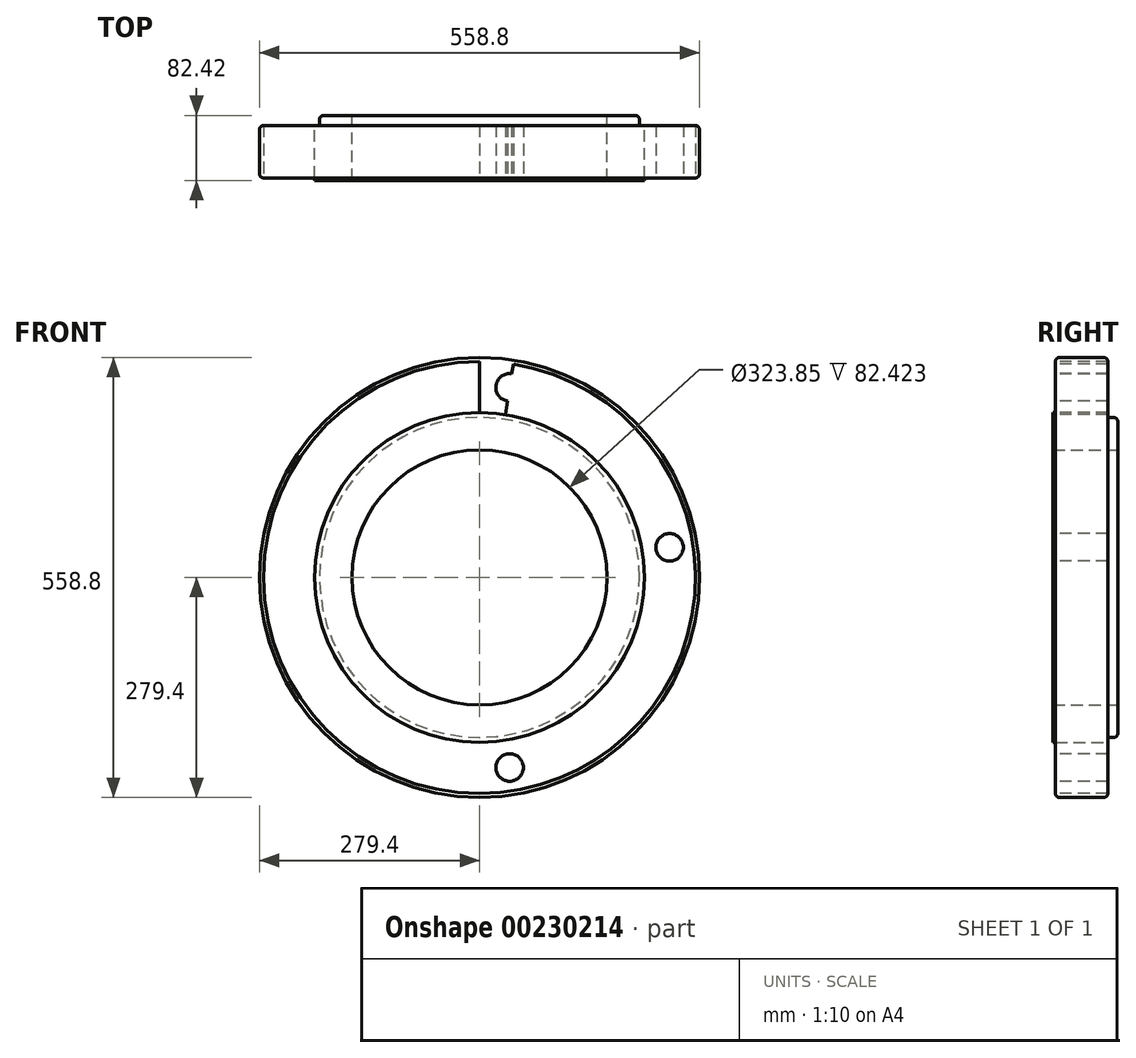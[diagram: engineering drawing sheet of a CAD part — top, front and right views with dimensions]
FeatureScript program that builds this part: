
annotation { "Feature Type Name" : "Feature", "Feature Type Description" : "" }
export const myFeature = defineFeature(function(context is Context, id is Id, definition is map)
    precondition{}
    {
        {
            var Q0;
            Q0=qCreatedBy(makeId("Front.planeOp"),FACE);
            var sketch = newSketch(context, id + "F0", { "sketchPlane" : qUnion([Q0])});
            skCircle(sketch, "E0", {"center": v(0, 0) * mm, "radius": 161.93 * mm});
            skCircle(sketch, "E1", {"center": v(0, 0) * mm, "radius": 279.4 * mm});
            skSolve(sketch);
        }
        {
            var Q0;
            Q0 = qSketchRegion(id + "F0", true);
            extrude(context, id + "F1", {"entities" : qUnion([Q0]), "depth" : 66.55 * mm});
        }
        {
            var Q0;
            Q0=makeQuery(id+"F1.opExtrude","CAP_FACE",FACE,{"disambiguationData":[OSD([sQuery(id+"F0.wireOp",EDGE,"E0"),sQuery(id+"F0.wireOp",EDGE,"E1")])],"isStart":false});
            var sketch = newSketch(context, id + "F2", { "sketchPlane" : qUnion([Q0])});
            skCircle(sketch, "E2", {"center": v(0, 0) * mm, "radius": 209.55 * mm});
            skCircle(sketch, "E3", {"center": v(0, 0) * mm, "radius": 161.93 * mm});
            skSolve(sketch);
        }
        {
            var Q0;
            Q0 = qSketchRegion(id + "F2", true);
            extrude(context, id + "F3", {"entities" : qUnion([Q0]), "operationType" : NewBodyOperationType.ADD, "depth" : 3.17 * mm});
        }
        {
            var Q0;
            Q0=makeQuery(id+"F1.opExtrude","CAP_FACE",FACE,{"disambiguationData":[OSD([sQuery(id+"F0.wireOp",EDGE,"E0"),sQuery(id+"F0.wireOp",EDGE,"E1")])],"isStart":true});
            var sketch = newSketch(context, id + "F4", { "sketchPlane" : qUnion([Q0])});
            skCircle(sketch, "E4", {"center": v(0, 0) * mm, "radius": 203.2 * mm});
            skCircle(sketch, "E5", {"center": v(0, 0) * mm, "radius": 161.93 * mm});
            skSolve(sketch);
        }
        {
            var Q0;
            Q0 = qSketchRegion(id + "F4", true);
            extrude(context, id + "F5", {"entities" : qUnion([Q0]), "operationType" : NewBodyOperationType.ADD, "depth" : 12.7 * mm});
        }
        {
            var Q0;
            Q0=makeQuery(id+"F1.opExtrude","CAP_EDGE",EDGE,{"disambiguationData":[OSD([sQuery(id+"F0.wireOp",EDGE,"E1")])],"isStart":true});
            var Q1;
            Q1=makeQuery(id+"F1.opExtrude","CAP_EDGE",EDGE,{"disambiguationData":[OSD([sQuery(id+"F0.wireOp",EDGE,"E1")])],"isStart":false});
            var Q2;
            Q2=makeQuery(id+"F5.opExtrude","CAP_EDGE",EDGE,{"disambiguationData":[OSD([sQuery(id+"F4.wireOp",EDGE,"E4")])],"isStart":false});
            var Q3;
            Q3=makeQuery(id+"F5.opExtrude","CAP_EDGE",EDGE,{"disambiguationData":[OSD([sQuery(id+"F4.wireOp",EDGE,"E4")])],"isStart":true});
            fillet(context, id + "F6", {"entities" : qUnion([Q0, Q1, Q2, Q3]), "radius" : 5.08 * mm, "tangentPropagation" : true, "allowEdgeOverflow" : false});
        }
        {
            var Q0;
            Q0=makeQuery(id+"F1.opExtrude","CAP_FACE",FACE,{"disambiguationData":[OSD([sQuery(id+"F0.wireOp",EDGE,"E0"),sQuery(id+"F0.wireOp",EDGE,"E1")])],"isStart":false});
            var sketch = newSketch(context, id + "F7", { "sketchPlane" : qUnion([Q0])});
            skCircle(sketch, "E6", {"center": v(0, 0) * mm, "radius": 244.48 * mm});
            skLineSegment(sketch, "E7", {"start": v(0, 0) * mm, "end": v(0, 331.7) * mm});
            skLineSegment(sketch, "E8", {"start": v(0, 0) * mm, "end": v(51.36, 324.26) * mm});
            skCircle(sketch, "E9", {"center": v(38.24, 241.47) * mm, "radius": 17.46 * mm});
            skCircle(sketch, "E10.1.0", {"center": v(-38.24, 241.47) * mm, "radius": 17.46 * mm});
            skCircle(sketch, "E10.2.0", {"center": v(-110.99, 217.83) * mm, "radius": 17.46 * mm});
            skCircle(sketch, "E10.3.0", {"center": v(-172.87, 172.87) * mm, "radius": 17.46 * mm});
            skCircle(sketch, "E10.4.0", {"center": v(-217.83, 110.99) * mm, "radius": 17.46 * mm});
            skCircle(sketch, "E10.5.0", {"center": v(-241.47, 38.24) * mm, "radius": 17.46 * mm});
            skCircle(sketch, "E10.6.0", {"center": v(-241.47, -38.24) * mm, "radius": 17.46 * mm});
            skCircle(sketch, "E10.7.0", {"center": v(-217.83, -110.99) * mm, "radius": 17.46 * mm});
            skCircle(sketch, "E10.8.0", {"center": v(-172.87, -172.87) * mm, "radius": 17.46 * mm});
            skCircle(sketch, "E10.9.0", {"center": v(-110.99, -217.83) * mm, "radius": 17.46 * mm});
            skCircle(sketch, "E10.10.0", {"center": v(-38.24, -241.47) * mm, "radius": 17.46 * mm});
            skCircle(sketch, "E10.11.0", {"center": v(38.24, -241.47) * mm, "radius": 17.46 * mm});
            skCircle(sketch, "E10.12.0", {"center": v(110.99, -217.83) * mm, "radius": 17.46 * mm});
            skCircle(sketch, "E10.13.0", {"center": v(172.87, -172.87) * mm, "radius": 17.46 * mm});
            skCircle(sketch, "E10.14.0", {"center": v(217.83, -110.99) * mm, "radius": 17.46 * mm});
            skCircle(sketch, "E10.15.0", {"center": v(241.47, -38.24) * mm, "radius": 17.46 * mm});
            skCircle(sketch, "E10.16.0", {"center": v(241.47, 38.24) * mm, "radius": 17.46 * mm});
            skCircle(sketch, "E10.17.0", {"center": v(217.83, 110.99) * mm, "radius": 17.46 * mm});
            skCircle(sketch, "E10.18.0", {"center": v(172.87, 172.87) * mm, "radius": 17.46 * mm});
            skCircle(sketch, "E10.19.0", {"center": v(110.99, 217.83) * mm, "radius": 17.46 * mm});
            skSolve(sketch);
        }
        {
            var Q0;
            {var subQ0=sQuery(id+"F7.wireOp",EDGE,"E10.16.0");var subQ1=sQuery(id+"F7.wireOp",EDGE,"E6");var subQ2=makeQuery(id+"F7.imprint","INTERSECT",VERTEX,{"disambiguationData":[OD(0.0)],"derivedFrom":[subQ1,subQ0]});Q0=makeQuery(id+"F7.imprint","IMPRINT",FACE,{"disambiguationData":[TD([[makeQuery(id+"F7.imprint","IMPRINT",EDGE,{"disambiguationData":[TD([[subQ2,1.0]])],"derivedFrom":subQ1}),1.0]])]});}
            var Q1;
            {var subQ0=sQuery(id+"F7.wireOp",EDGE,"E10.16.0");var subQ1=sQuery(id+"F7.wireOp",EDGE,"E6");var subQ2=makeQuery(id+"F7.imprint","INTERSECT",VERTEX,{"disambiguationData":[OD(0.0)],"derivedFrom":[subQ1,subQ0]});Q1=makeQuery(id+"F7.imprint","IMPRINT",FACE,{"disambiguationData":[TD([[makeQuery(id+"F7.imprint","IMPRINT",EDGE,{"disambiguationData":[TD([[subQ2,1.0]])],"derivedFrom":subQ1}),-1.0]])]});}
            var Q2;
            {var subQ0=sQuery(id+"F7.wireOp",EDGE,"E10.17.0");var subQ1=sQuery(id+"F7.wireOp",EDGE,"E6");var subQ2=makeQuery(id+"F7.imprint","INTERSECT",VERTEX,{"disambiguationData":[OD(0.0)],"derivedFrom":[subQ1,subQ0]});Q2=makeQuery(id+"F7.imprint","IMPRINT",FACE,{"disambiguationData":[TD([[makeQuery(id+"F7.imprint","IMPRINT",EDGE,{"disambiguationData":[TD([[subQ2,-1.0]])],"derivedFrom":subQ1}),1.0]])]});}
            var Q3;
            {var subQ0=sQuery(id+"F7.wireOp",EDGE,"E10.17.0");var subQ1=sQuery(id+"F7.wireOp",EDGE,"E6");var subQ2=makeQuery(id+"F7.imprint","INTERSECT",VERTEX,{"disambiguationData":[OD(0.0)],"derivedFrom":[subQ1,subQ0]});Q3=makeQuery(id+"F7.imprint","IMPRINT",FACE,{"disambiguationData":[TD([[makeQuery(id+"F7.imprint","IMPRINT",EDGE,{"disambiguationData":[TD([[subQ2,-1.0]])],"derivedFrom":subQ1}),-1.0]])]});}
            var Q4;
            {var subQ0=sQuery(id+"F7.wireOp",EDGE,"E10.18.0");var subQ1=sQuery(id+"F7.wireOp",EDGE,"E6");var subQ2=makeQuery(id+"F7.imprint","INTERSECT",VERTEX,{"disambiguationData":[OD(0.0)],"derivedFrom":[subQ1,subQ0]});Q4=makeQuery(id+"F7.imprint","IMPRINT",FACE,{"disambiguationData":[TD([[makeQuery(id+"F7.imprint","IMPRINT",EDGE,{"disambiguationData":[TD([[subQ2,-1.0]])],"derivedFrom":subQ1}),1.0]])]});}
            var Q5;
            {var subQ0=sQuery(id+"F7.wireOp",EDGE,"E10.18.0");var subQ1=sQuery(id+"F7.wireOp",EDGE,"E6");var subQ2=makeQuery(id+"F7.imprint","INTERSECT",VERTEX,{"disambiguationData":[OD(0.0)],"derivedFrom":[subQ1,subQ0]});Q5=makeQuery(id+"F7.imprint","IMPRINT",FACE,{"disambiguationData":[TD([[makeQuery(id+"F7.imprint","IMPRINT",EDGE,{"disambiguationData":[TD([[subQ2,-1.0]])],"derivedFrom":subQ1}),-1.0]])]});}
            var Q6;
            {var subQ0=sQuery(id+"F7.wireOp",EDGE,"E10.19.0");var subQ1=sQuery(id+"F7.wireOp",EDGE,"E6");var subQ2=makeQuery(id+"F7.imprint","INTERSECT",VERTEX,{"disambiguationData":[OD(0.0)],"derivedFrom":[subQ1,subQ0]});Q6=makeQuery(id+"F7.imprint","IMPRINT",FACE,{"disambiguationData":[TD([[makeQuery(id+"F7.imprint","IMPRINT",EDGE,{"disambiguationData":[TD([[subQ2,-1.0]])],"derivedFrom":subQ1}),1.0]])]});}
            var Q7;
            {var subQ0=sQuery(id+"F7.wireOp",EDGE,"E10.19.0");var subQ1=sQuery(id+"F7.wireOp",EDGE,"E6");var subQ2=makeQuery(id+"F7.imprint","INTERSECT",VERTEX,{"disambiguationData":[OD(0.0)],"derivedFrom":[subQ1,subQ0]});Q7=makeQuery(id+"F7.imprint","IMPRINT",FACE,{"disambiguationData":[TD([[makeQuery(id+"F7.imprint","IMPRINT",EDGE,{"disambiguationData":[TD([[subQ2,-1.0]])],"derivedFrom":subQ1}),-1.0]])]});}
            var Q8;
            {var subQ0=sQuery(id+"F7.wireOp",EDGE,"E10.1.0");var subQ1=sQuery(id+"F7.wireOp",EDGE,"E6");var subQ2=makeQuery(id+"F7.imprint","INTERSECT",VERTEX,{"disambiguationData":[OD(0.0)],"derivedFrom":[subQ1,subQ0]});Q8=makeQuery(id+"F7.imprint","IMPRINT",FACE,{"disambiguationData":[TD([[makeQuery(id+"F7.imprint","IMPRINT",EDGE,{"disambiguationData":[TD([[subQ2,-1.0]])],"derivedFrom":subQ1}),1.0]])]});}
            var Q9;
            {var subQ0=sQuery(id+"F7.wireOp",EDGE,"E10.1.0");var subQ1=sQuery(id+"F7.wireOp",EDGE,"E6");var subQ2=makeQuery(id+"F7.imprint","INTERSECT",VERTEX,{"disambiguationData":[OD(0.0)],"derivedFrom":[subQ1,subQ0]});Q9=makeQuery(id+"F7.imprint","IMPRINT",FACE,{"disambiguationData":[TD([[makeQuery(id+"F7.imprint","IMPRINT",EDGE,{"disambiguationData":[TD([[subQ2,-1.0]])],"derivedFrom":subQ1}),-1.0]])]});}
            var Q10;
            {var subQ0=sQuery(id+"F7.wireOp",EDGE,"E10.2.0");var subQ1=sQuery(id+"F7.wireOp",EDGE,"E6");var subQ2=makeQuery(id+"F7.imprint","INTERSECT",VERTEX,{"disambiguationData":[OD(0.0)],"derivedFrom":[subQ1,subQ0]});Q10=makeQuery(id+"F7.imprint","IMPRINT",FACE,{"disambiguationData":[TD([[makeQuery(id+"F7.imprint","IMPRINT",EDGE,{"disambiguationData":[TD([[subQ2,-1.0]])],"derivedFrom":subQ1}),1.0]])]});}
            var Q11;
            {var subQ0=sQuery(id+"F7.wireOp",EDGE,"E10.2.0");var subQ1=sQuery(id+"F7.wireOp",EDGE,"E6");var subQ2=makeQuery(id+"F7.imprint","INTERSECT",VERTEX,{"disambiguationData":[OD(0.0)],"derivedFrom":[subQ1,subQ0]});Q11=makeQuery(id+"F7.imprint","IMPRINT",FACE,{"disambiguationData":[TD([[makeQuery(id+"F7.imprint","IMPRINT",EDGE,{"disambiguationData":[TD([[subQ2,-1.0]])],"derivedFrom":subQ1}),-1.0]])]});}
            var Q12;
            {var subQ0=sQuery(id+"F7.wireOp",EDGE,"E10.3.0");var subQ1=sQuery(id+"F7.wireOp",EDGE,"E6");var subQ2=makeQuery(id+"F7.imprint","INTERSECT",VERTEX,{"disambiguationData":[OD(0.0)],"derivedFrom":[subQ1,subQ0]});Q12=makeQuery(id+"F7.imprint","IMPRINT",FACE,{"disambiguationData":[TD([[makeQuery(id+"F7.imprint","IMPRINT",EDGE,{"disambiguationData":[TD([[subQ2,-1.0]])],"derivedFrom":subQ1}),1.0]])]});}
            var Q13;
            {var subQ0=sQuery(id+"F7.wireOp",EDGE,"E10.3.0");var subQ1=sQuery(id+"F7.wireOp",EDGE,"E6");var subQ2=makeQuery(id+"F7.imprint","INTERSECT",VERTEX,{"disambiguationData":[OD(0.0)],"derivedFrom":[subQ1,subQ0]});Q13=makeQuery(id+"F7.imprint","IMPRINT",FACE,{"disambiguationData":[TD([[makeQuery(id+"F7.imprint","IMPRINT",EDGE,{"disambiguationData":[TD([[subQ2,-1.0]])],"derivedFrom":subQ1}),-1.0]])]});}
            var Q14;
            {var subQ0=sQuery(id+"F7.wireOp",EDGE,"E10.4.0");var subQ1=sQuery(id+"F7.wireOp",EDGE,"E6");var subQ2=makeQuery(id+"F7.imprint","INTERSECT",VERTEX,{"disambiguationData":[OD(0.0)],"derivedFrom":[subQ1,subQ0]});Q14=makeQuery(id+"F7.imprint","IMPRINT",FACE,{"disambiguationData":[TD([[makeQuery(id+"F7.imprint","IMPRINT",EDGE,{"disambiguationData":[TD([[subQ2,-1.0]])],"derivedFrom":subQ1}),1.0]])]});}
            var Q15;
            {var subQ0=sQuery(id+"F7.wireOp",EDGE,"E10.4.0");var subQ1=sQuery(id+"F7.wireOp",EDGE,"E6");var subQ2=makeQuery(id+"F7.imprint","INTERSECT",VERTEX,{"disambiguationData":[OD(0.0)],"derivedFrom":[subQ1,subQ0]});Q15=makeQuery(id+"F7.imprint","IMPRINT",FACE,{"disambiguationData":[TD([[makeQuery(id+"F7.imprint","IMPRINT",EDGE,{"disambiguationData":[TD([[subQ2,-1.0]])],"derivedFrom":subQ1}),-1.0]])]});}
            var Q16;
            {var subQ0=sQuery(id+"F7.wireOp",EDGE,"E10.5.0");var subQ1=sQuery(id+"F7.wireOp",EDGE,"E6");var subQ2=makeQuery(id+"F7.imprint","INTERSECT",VERTEX,{"disambiguationData":[OD(0.0)],"derivedFrom":[subQ1,subQ0]});Q16=makeQuery(id+"F7.imprint","IMPRINT",FACE,{"disambiguationData":[TD([[makeQuery(id+"F7.imprint","IMPRINT",EDGE,{"disambiguationData":[TD([[subQ2,-1.0]])],"derivedFrom":subQ1}),1.0]])]});}
            var Q17;
            {var subQ0=sQuery(id+"F7.wireOp",EDGE,"E10.5.0");var subQ1=sQuery(id+"F7.wireOp",EDGE,"E6");var subQ2=makeQuery(id+"F7.imprint","INTERSECT",VERTEX,{"disambiguationData":[OD(0.0)],"derivedFrom":[subQ1,subQ0]});Q17=makeQuery(id+"F7.imprint","IMPRINT",FACE,{"disambiguationData":[TD([[makeQuery(id+"F7.imprint","IMPRINT",EDGE,{"disambiguationData":[TD([[subQ2,-1.0]])],"derivedFrom":subQ1}),-1.0]])]});}
            var Q18;
            {var subQ0=sQuery(id+"F7.wireOp",EDGE,"E10.6.0");var subQ1=sQuery(id+"F7.wireOp",EDGE,"E6");var subQ2=makeQuery(id+"F7.imprint","INTERSECT",VERTEX,{"disambiguationData":[OD(0.0)],"derivedFrom":[subQ1,subQ0]});Q18=makeQuery(id+"F7.imprint","IMPRINT",FACE,{"disambiguationData":[TD([[makeQuery(id+"F7.imprint","IMPRINT",EDGE,{"disambiguationData":[TD([[subQ2,-1.0]])],"derivedFrom":subQ1}),1.0]])]});}
            var Q19;
            {var subQ0=sQuery(id+"F7.wireOp",EDGE,"E10.6.0");var subQ1=sQuery(id+"F7.wireOp",EDGE,"E6");var subQ2=makeQuery(id+"F7.imprint","INTERSECT",VERTEX,{"disambiguationData":[OD(0.0)],"derivedFrom":[subQ1,subQ0]});Q19=makeQuery(id+"F7.imprint","IMPRINT",FACE,{"disambiguationData":[TD([[makeQuery(id+"F7.imprint","IMPRINT",EDGE,{"disambiguationData":[TD([[subQ2,-1.0]])],"derivedFrom":subQ1}),-1.0]])]});}
            var Q20;
            {var subQ0=sQuery(id+"F7.wireOp",EDGE,"E10.7.0");var subQ1=sQuery(id+"F7.wireOp",EDGE,"E6");var subQ2=makeQuery(id+"F7.imprint","INTERSECT",VERTEX,{"disambiguationData":[OD(0.0)],"derivedFrom":[subQ1,subQ0]});Q20=makeQuery(id+"F7.imprint","IMPRINT",FACE,{"disambiguationData":[TD([[makeQuery(id+"F7.imprint","IMPRINT",EDGE,{"disambiguationData":[TD([[subQ2,-1.0]])],"derivedFrom":subQ1}),1.0]])]});}
            var Q21;
            {var subQ0=sQuery(id+"F7.wireOp",EDGE,"E10.7.0");var subQ1=sQuery(id+"F7.wireOp",EDGE,"E6");var subQ2=makeQuery(id+"F7.imprint","INTERSECT",VERTEX,{"disambiguationData":[OD(0.0)],"derivedFrom":[subQ1,subQ0]});Q21=makeQuery(id+"F7.imprint","IMPRINT",FACE,{"disambiguationData":[TD([[makeQuery(id+"F7.imprint","IMPRINT",EDGE,{"disambiguationData":[TD([[subQ2,-1.0]])],"derivedFrom":subQ1}),-1.0]])]});}
            var Q22;
            {var subQ0=sQuery(id+"F7.wireOp",EDGE,"E10.8.0");var subQ1=sQuery(id+"F7.wireOp",EDGE,"E6");var subQ2=makeQuery(id+"F7.imprint","INTERSECT",VERTEX,{"disambiguationData":[OD(0.0)],"derivedFrom":[subQ1,subQ0]});Q22=makeQuery(id+"F7.imprint","IMPRINT",FACE,{"disambiguationData":[TD([[makeQuery(id+"F7.imprint","IMPRINT",EDGE,{"disambiguationData":[TD([[subQ2,-1.0]])],"derivedFrom":subQ1}),1.0]])]});}
            var Q23;
            {var subQ0=sQuery(id+"F7.wireOp",EDGE,"E10.8.0");var subQ1=sQuery(id+"F7.wireOp",EDGE,"E6");var subQ2=makeQuery(id+"F7.imprint","INTERSECT",VERTEX,{"disambiguationData":[OD(0.0)],"derivedFrom":[subQ1,subQ0]});Q23=makeQuery(id+"F7.imprint","IMPRINT",FACE,{"disambiguationData":[TD([[makeQuery(id+"F7.imprint","IMPRINT",EDGE,{"disambiguationData":[TD([[subQ2,-1.0]])],"derivedFrom":subQ1}),-1.0]])]});}
            var Q24;
            {var subQ0=sQuery(id+"F7.wireOp",EDGE,"E10.9.0");var subQ1=sQuery(id+"F7.wireOp",EDGE,"E6");var subQ2=makeQuery(id+"F7.imprint","INTERSECT",VERTEX,{"disambiguationData":[OD(0.0)],"derivedFrom":[subQ1,subQ0]});Q24=makeQuery(id+"F7.imprint","IMPRINT",FACE,{"disambiguationData":[TD([[makeQuery(id+"F7.imprint","IMPRINT",EDGE,{"disambiguationData":[TD([[subQ2,-1.0]])],"derivedFrom":subQ1}),1.0]])]});}
            var Q25;
            {var subQ0=sQuery(id+"F7.wireOp",EDGE,"E10.9.0");var subQ1=sQuery(id+"F7.wireOp",EDGE,"E6");var subQ2=makeQuery(id+"F7.imprint","INTERSECT",VERTEX,{"disambiguationData":[OD(0.0)],"derivedFrom":[subQ1,subQ0]});Q25=makeQuery(id+"F7.imprint","IMPRINT",FACE,{"disambiguationData":[TD([[makeQuery(id+"F7.imprint","IMPRINT",EDGE,{"disambiguationData":[TD([[subQ2,-1.0]])],"derivedFrom":subQ1}),-1.0]])]});}
            var Q26;
            {var subQ0=sQuery(id+"F7.wireOp",EDGE,"E10.10.0");var subQ1=sQuery(id+"F7.wireOp",EDGE,"E6");var subQ2=makeQuery(id+"F7.imprint","INTERSECT",VERTEX,{"disambiguationData":[OD(0.0)],"derivedFrom":[subQ1,subQ0]});Q26=makeQuery(id+"F7.imprint","IMPRINT",FACE,{"disambiguationData":[TD([[makeQuery(id+"F7.imprint","IMPRINT",EDGE,{"disambiguationData":[TD([[subQ2,-1.0]])],"derivedFrom":subQ1}),1.0]])]});}
            var Q27;
            {var subQ0=sQuery(id+"F7.wireOp",EDGE,"E10.10.0");var subQ1=sQuery(id+"F7.wireOp",EDGE,"E6");var subQ2=makeQuery(id+"F7.imprint","INTERSECT",VERTEX,{"disambiguationData":[OD(0.0)],"derivedFrom":[subQ1,subQ0]});Q27=makeQuery(id+"F7.imprint","IMPRINT",FACE,{"disambiguationData":[TD([[makeQuery(id+"F7.imprint","IMPRINT",EDGE,{"disambiguationData":[TD([[subQ2,-1.0]])],"derivedFrom":subQ1}),-1.0]])]});}
            var Q28;
            {var subQ0=sQuery(id+"F7.wireOp",EDGE,"E10.11.0");var subQ1=sQuery(id+"F7.wireOp",EDGE,"E6");var subQ2=makeQuery(id+"F7.imprint","INTERSECT",VERTEX,{"disambiguationData":[OD(0.0)],"derivedFrom":[subQ1,subQ0]});Q28=makeQuery(id+"F7.imprint","IMPRINT",FACE,{"disambiguationData":[TD([[makeQuery(id+"F7.imprint","IMPRINT",EDGE,{"disambiguationData":[TD([[subQ2,-1.0]])],"derivedFrom":subQ1}),1.0]])]});}
            var Q29;
            {var subQ0=sQuery(id+"F7.wireOp",EDGE,"E10.11.0");var subQ1=sQuery(id+"F7.wireOp",EDGE,"E6");var subQ2=makeQuery(id+"F7.imprint","INTERSECT",VERTEX,{"disambiguationData":[OD(0.0)],"derivedFrom":[subQ1,subQ0]});Q29=makeQuery(id+"F7.imprint","IMPRINT",FACE,{"disambiguationData":[TD([[makeQuery(id+"F7.imprint","IMPRINT",EDGE,{"disambiguationData":[TD([[subQ2,-1.0]])],"derivedFrom":subQ1}),-1.0]])]});}
            var Q30;
            {var subQ0=sQuery(id+"F7.wireOp",EDGE,"E10.12.0");var subQ1=sQuery(id+"F7.wireOp",EDGE,"E6");var subQ2=makeQuery(id+"F7.imprint","INTERSECT",VERTEX,{"disambiguationData":[OD(0.0)],"derivedFrom":[subQ1,subQ0]});Q30=makeQuery(id+"F7.imprint","IMPRINT",FACE,{"disambiguationData":[TD([[makeQuery(id+"F7.imprint","IMPRINT",EDGE,{"disambiguationData":[TD([[subQ2,-1.0]])],"derivedFrom":subQ1}),1.0]])]});}
            var Q31;
            {var subQ0=sQuery(id+"F7.wireOp",EDGE,"E10.12.0");var subQ1=sQuery(id+"F7.wireOp",EDGE,"E6");var subQ2=makeQuery(id+"F7.imprint","INTERSECT",VERTEX,{"disambiguationData":[OD(0.0)],"derivedFrom":[subQ1,subQ0]});Q31=makeQuery(id+"F7.imprint","IMPRINT",FACE,{"disambiguationData":[TD([[makeQuery(id+"F7.imprint","IMPRINT",EDGE,{"disambiguationData":[TD([[subQ2,-1.0]])],"derivedFrom":subQ1}),-1.0]])]});}
            var Q32;
            {var subQ0=sQuery(id+"F7.wireOp",EDGE,"E10.13.0");var subQ1=sQuery(id+"F7.wireOp",EDGE,"E6");var subQ2=makeQuery(id+"F7.imprint","INTERSECT",VERTEX,{"disambiguationData":[OD(0.0)],"derivedFrom":[subQ1,subQ0]});Q32=makeQuery(id+"F7.imprint","IMPRINT",FACE,{"disambiguationData":[TD([[makeQuery(id+"F7.imprint","IMPRINT",EDGE,{"disambiguationData":[TD([[subQ2,-1.0]])],"derivedFrom":subQ1}),1.0]])]});}
            var Q33;
            {var subQ0=sQuery(id+"F7.wireOp",EDGE,"E10.13.0");var subQ1=sQuery(id+"F7.wireOp",EDGE,"E6");var subQ2=makeQuery(id+"F7.imprint","INTERSECT",VERTEX,{"disambiguationData":[OD(0.0)],"derivedFrom":[subQ1,subQ0]});Q33=makeQuery(id+"F7.imprint","IMPRINT",FACE,{"disambiguationData":[TD([[makeQuery(id+"F7.imprint","IMPRINT",EDGE,{"disambiguationData":[TD([[subQ2,-1.0]])],"derivedFrom":subQ1}),-1.0]])]});}
            var Q34;
            {var subQ0=sQuery(id+"F7.wireOp",EDGE,"E10.14.0");var subQ1=sQuery(id+"F7.wireOp",EDGE,"E6");var subQ2=makeQuery(id+"F7.imprint","INTERSECT",VERTEX,{"disambiguationData":[OD(0.0)],"derivedFrom":[subQ1,subQ0]});Q34=makeQuery(id+"F7.imprint","IMPRINT",FACE,{"disambiguationData":[TD([[makeQuery(id+"F7.imprint","IMPRINT",EDGE,{"disambiguationData":[TD([[subQ2,-1.0]])],"derivedFrom":subQ1}),1.0]])]});}
            var Q35;
            {var subQ0=sQuery(id+"F7.wireOp",EDGE,"E10.14.0");var subQ1=sQuery(id+"F7.wireOp",EDGE,"E6");var subQ2=makeQuery(id+"F7.imprint","INTERSECT",VERTEX,{"disambiguationData":[OD(0.0)],"derivedFrom":[subQ1,subQ0]});Q35=makeQuery(id+"F7.imprint","IMPRINT",FACE,{"disambiguationData":[TD([[makeQuery(id+"F7.imprint","IMPRINT",EDGE,{"disambiguationData":[TD([[subQ2,-1.0]])],"derivedFrom":subQ1}),-1.0]])]});}
            var Q36;
            {var subQ0=sQuery(id+"F7.wireOp",EDGE,"E10.15.0");var subQ1=sQuery(id+"F7.wireOp",EDGE,"E6");var subQ2=makeQuery(id+"F7.imprint","INTERSECT",VERTEX,{"disambiguationData":[OD(0.0)],"derivedFrom":[subQ1,subQ0]});Q36=makeQuery(id+"F7.imprint","IMPRINT",FACE,{"disambiguationData":[TD([[makeQuery(id+"F7.imprint","IMPRINT",EDGE,{"disambiguationData":[TD([[subQ2,-1.0]])],"derivedFrom":subQ1}),1.0]])]});}
            var Q37;
            {var subQ0=sQuery(id+"F7.wireOp",EDGE,"E10.15.0");var subQ1=sQuery(id+"F7.wireOp",EDGE,"E6");var subQ2=makeQuery(id+"F7.imprint","INTERSECT",VERTEX,{"disambiguationData":[OD(0.0)],"derivedFrom":[subQ1,subQ0]});Q37=makeQuery(id+"F7.imprint","IMPRINT",FACE,{"disambiguationData":[TD([[makeQuery(id+"F7.imprint","IMPRINT",EDGE,{"disambiguationData":[TD([[subQ2,-1.0]])],"derivedFrom":subQ1}),-1.0]])]});}
            var Q38;
            {var subQ0=sQuery(id+"F7.wireOp",EDGE,"E9");var subQ1=sQuery(id+"F7.wireOp",EDGE,"E6");var subQ2=makeQuery(id+"F7.imprint","INTERSECT",VERTEX,{"disambiguationData":[OD(0.0)],"derivedFrom":[subQ1,subQ0]});Q38=makeQuery(id+"F7.imprint","IMPRINT",FACE,{"disambiguationData":[TD([[makeQuery(id+"F7.imprint","IMPRINT",EDGE,{"disambiguationData":[TD([[subQ2,-1.0]])],"derivedFrom":subQ1}),1.0]])]});}
            var Q39;
            {var subQ0=sQuery(id+"F7.wireOp",EDGE,"E9");var subQ1=sQuery(id+"F7.wireOp",EDGE,"E6");var subQ2=makeQuery(id+"F7.imprint","INTERSECT",VERTEX,{"disambiguationData":[OD(0.0)],"derivedFrom":[subQ1,subQ0]});Q39=makeQuery(id+"F7.imprint","IMPRINT",FACE,{"disambiguationData":[TD([[makeQuery(id+"F7.imprint","IMPRINT",EDGE,{"disambiguationData":[TD([[subQ2,-1.0]])],"derivedFrom":subQ1}),-1.0]])]});}
            var Q40;
            {var subQ0=sQuery(id+"F7.wireOp",EDGE,"E8");var subQ1=sQuery(id+"F7.wireOp",EDGE,"E6");var subQ2=makeQuery(id+"F7.imprint","INTERSECT",VERTEX,{"derivedFrom":[subQ1,subQ0]});Q40=makeQuery(id+"F7.imprint","IMPRINT",FACE,{"disambiguationData":[TD([[makeQuery(id+"F7.imprint","IMPRINT",EDGE,{"disambiguationData":[TD([[subQ2,-1.0]])],"derivedFrom":subQ1}),1.0]])]});}
            var Q41;
            {var subQ0=sQuery(id+"F7.wireOp",EDGE,"E8");var subQ1=sQuery(id+"F7.wireOp",EDGE,"E6");var subQ2=makeQuery(id+"F7.imprint","INTERSECT",VERTEX,{"derivedFrom":[subQ1,subQ0]});Q41=makeQuery(id+"F7.imprint","IMPRINT",FACE,{"disambiguationData":[TD([[makeQuery(id+"F7.imprint","IMPRINT",EDGE,{"disambiguationData":[TD([[subQ2,-1.0]])],"derivedFrom":subQ1}),-1.0]])]});}
            extrude(context, id + "F8", {"entities" : qUnion([Q0, Q1, Q2, Q3, Q4, Q5, Q6, Q7, Q8, Q9, Q10, Q11, Q12, Q13, Q14, Q15, Q16, Q17, Q18, Q19, Q20, Q21, Q22, Q23, Q24, Q25, Q26, Q27, Q28, Q29, Q30, Q31, Q32, Q33, Q34, Q35, Q36, Q37, Q38, Q39, Q40, Q41]), "operationType" : NewBodyOperationType.REMOVE, "oppositeDirection" : true, "depth" : 76.2 * mm});
        }
    });
